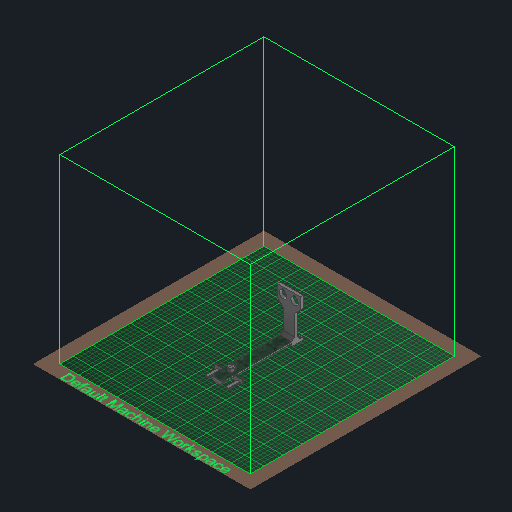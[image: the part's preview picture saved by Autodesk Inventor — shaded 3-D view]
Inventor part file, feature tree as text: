
AUTODESK INVENTOR PART (.ipt)
format: ipt  version: 2022 (Build 260153000, 153)  size: 718,848 bytes
history: native  units: in
note: dims shown in document units (in); Inventor stores cm internally (conversion verified against a paired STEP export)
features: sketch x17, extrude x15, projected_geometry x9, chamfer x7, reference x5, other x4, fillet x1
ambient origin geometry x8: Origin, YZ Plane, XZ Plane, XY Plane, X Axis, Y Axis, Z Axis, Center Point
bodies: Solid1 (feature_tree)
feature tree (58):
  extrude  "Extrusion1"  Depth=6.5in
  extrude  "Extrusion2"  Depth=1.031in
  extrude  "Extrusion3"  Depth=0.25in TaperAngle=0.0deg
  chamfer  "Chamfer1"  Distance=0.25in
  extrude  "Extrusion5"  Depth=0.025in
  extrude  "Extrusion6"  Depth=0.025in
  extrude  "Extrusion7"  Depth=0.1in
  extrude  "Extrusion8"  Depth=0.495in
  sketch  "Sketch9"  dims[d33=0.4936in d34=0.25in d35=3.5in d36=0.0in]
  extrude  "Extrusion9"  Depth=0.25in
  chamfer  "Chamfer6"  Distance=3.5in
  extrude  "Extrusion10"  Depth=0.5in TaperAngle=0.0deg
  extrude  "Extrusion12"  Depth=0.25in
  extrude  "Extrusion13"  Depth=0.5in
  fillet  "Fillet1"  Radius=0.176in
  sketch  "Sketch14"  dims[d51=0.32in d52=0.64in]
  extrude  "Extrusion14"  Depth=0.32in
  extrude  "Extrusion15"  Depth=1.0in
  chamfer  "Chamfer11"  Distance=0.25in
  chamfer  "Chamfer12"  Distance=0.25in Angle=45.0deg
  chamfer  "Chamfer13"  Distance=1.0in
  sketch  "Sketch20"  dims[d85=0.125in d86=0.2in]
  extrude  "Extrusion18"  Depth=0.125in
  chamfer  "Chamfer14"  Distance=0.125in
  extrude  "Extrusion20"  Depth=0.2in
  chamfer  "Chamfer17"  Distance=1.0in
  sketch  "Sketch1"  dims[d0=1.0in d1=6.5in]
  sketch  "Sketch2"  dims[d2=0.495in d3=1.031in]
  projected_geometry  "Projected Loop1"
  sketch  "Sketch3"  dims[d4=0.125in d5=0.0in d6=0.25in d7=0.125in d8=0.0in d9=0.0in d10=0.25in d11=0.0in]
  projected_geometry  "Projected Loop2"
  sketch  "Sketch5"  dims[d12=0.25in d13=0.125in d14=45.0deg d25=0.025in]
  reference  "Reference1"
  reference  "Reference2"
  reference  "Reference3"
  sketch  "Sketch6"  dims[d26=0.05in d27=0.025in]
  projected_geometry  "Projected Loop3"
  sketch  "Sketch7"  dims[d28=0.05in d29=0.1in]
  sketch  "Sketch8"  dims[d30=0.5in d31=0.0in d32=0.495in]
  reference  "Reference4"
  reference  "Reference5"
  sketch  "Sketch10"  dims[d37=1.0in d38=0.5in d39=0.0in]
  projected_geometry  "Projected Loop4"
  sketch  "Sketch12"  dims[d40=1.0in d41=0.25in]
  projected_geometry  "Projected Loop5"
  sketch  "Sketch13"  dims[d42=0.5in d43=0.0in d49=1.0079in d50=0.176in]
  projected_geometry  "Projected Loop6"
  projected_geometry  "Projected Loop7"
  sketch  "Sketch15"  dims[d53=0.496in d54=0.64in d55=0.25in d56=0.0in d60=0.25in d61=0.125in d62=45.0deg d63=1.0in d64=0.0in]
  sketch  "Sketch16"  dims[d74=1.225in d75=1.225in d76=0.125in d77=0.0in]
  projected_geometry  "Projected Loop8"
  projected_geometry  "Projected Loop9"
  sketch  "Sketch21"  dims[d87=0.495in d88=1.0in d89=0.0in]
  sketch  "Sketch23"  dims[d90=0.125in d91=0.125in d92=0.2in d93=0.5in d94=0.125in d95=0.0in d96=0.125in d97=0.0in d107=0.025in d108=0.125in d109=45.0deg d110=0.025in d111=0.125in d112=45.0deg d113=0.025in d114=0.125in d115=45.0deg d125=0.2in d126=0.0in d127=0.5in d128=0.125in d129=45.0deg d138=0.5in d139=0.1in d140=0.25in d141=0.0in d142=0.25in d143=0.125in d144=45.0deg d123=0.5in d124=0.0344in]
  parser-record x1  (decoder bookkeeping rows leaked as tree rows — omitted from the tree; the rows remain in map.json)
  other  "Prototype Assembly.iam"
  other  "Base:1"
  other  "hc-sr04:1"
note: 1 file-system path scrubbed to <path> (originals preserved in map.json)
